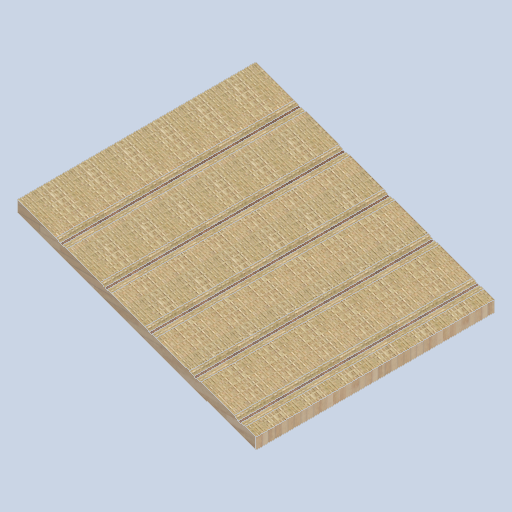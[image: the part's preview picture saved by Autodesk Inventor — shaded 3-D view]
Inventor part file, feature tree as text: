
AUTODESK INVENTOR PART (.ipt)
format: ipt  version: 2024.2 (Build 282272000, 272)  size: 544,768 bytes
history: native  units: mm
features: sketch x4, plane x3, extrude x2, fillet x1
ambient origin geometry x8: Origin, YZ Plane, XZ Plane, XY Plane, X Axis, Y Axis, Z Axis, Center Point
bodies: Solid1 (feature_tree)
feature tree (10):
  sketch  "Sketch1"  dims[d0=100.0mm d1=2111.0mm]
  plane  "Work Plane2"
  sketch  "Sketch3"  dims[d2=0.0mm d3=2109.0mm d4=19.198622mm d5=19.198622mm]
  plane  "Work Plane3"
  extrude  "Extrusion1"  Depth=2111.0mm
  extrude  "Extrusion2"  Depth=2109.0mm
  fillet  "Fillet1"  Radius=19.198622mm
  plane  "Work Plane1"
  sketch  "Sketch4"  dims[d6=2111.0mm d7=0.0mm]
  sketch  "Sketch5"  dims[d8=400.0mm d9=10.0mm d10=20.0mm d11=400.0mm d12=20.0mm d13=400.0mm d14=20.0mm d15=400.0mm d16=20.0mm d17=400.0mm d18=20.0mm d19=0.0mm d20=0.0mm d21=100.0mm]
